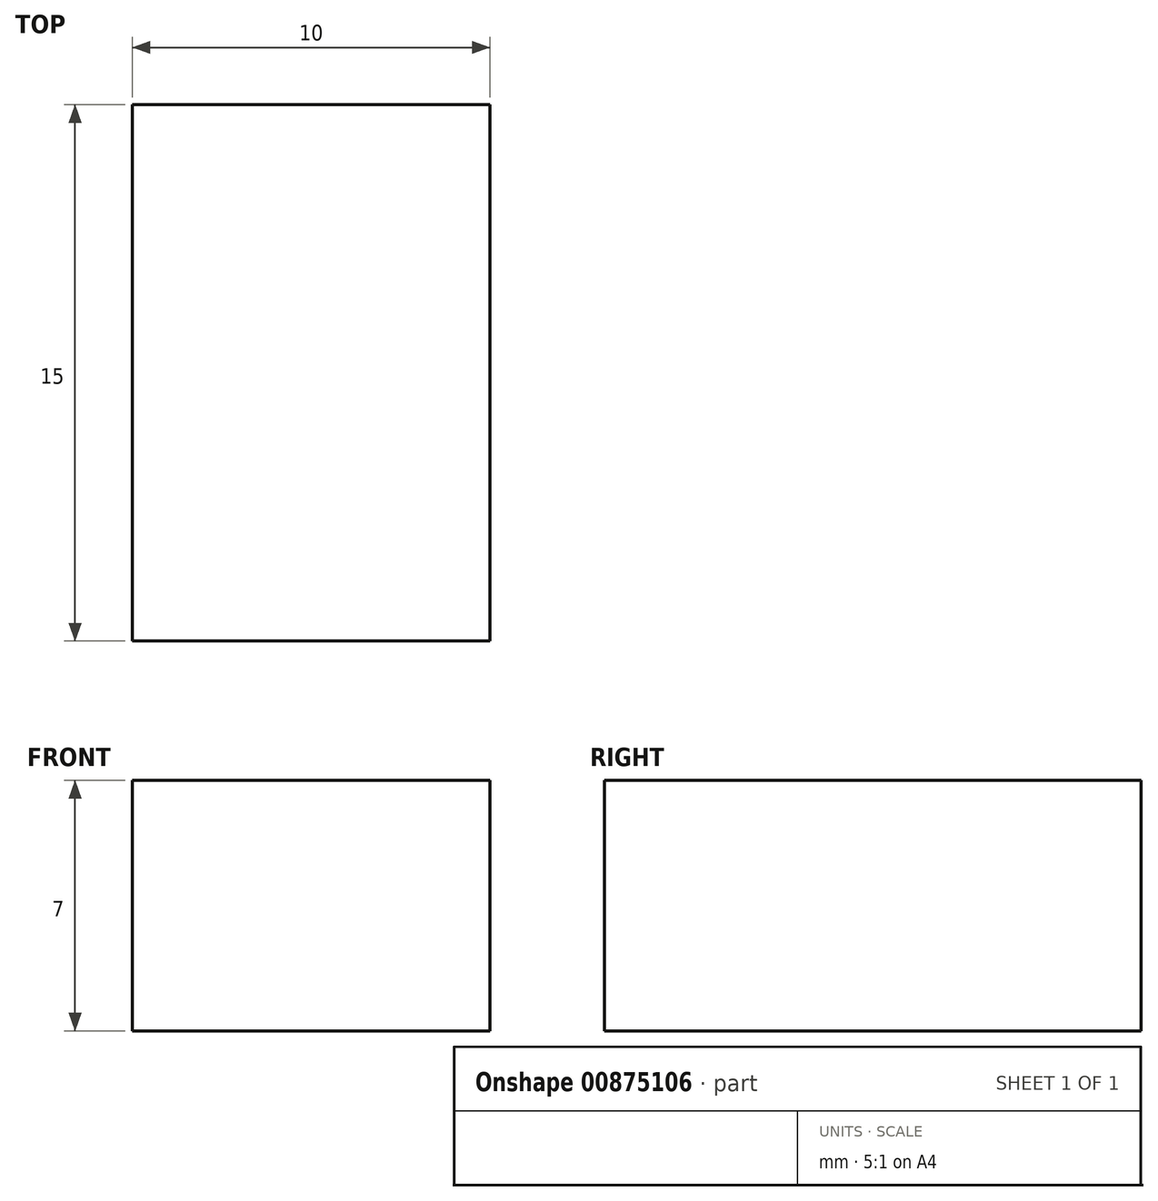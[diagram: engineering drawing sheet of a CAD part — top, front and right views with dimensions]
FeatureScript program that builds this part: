
annotation { "Feature Type Name" : "Feature", "Feature Type Description" : "" }
export const myFeature = defineFeature(function(context is Context, id is Id, definition is map)
    precondition{}
    {
        {
            var Q0;
            Q0=qCreatedBy(makeId("Top.planeOp"),FACE);
            var sketch = newSketch(context, id + "F0", { "sketchPlane" : qUnion([Q0])});
            skLineSegment(sketch, "E0.bottom", {"start": v(0, 0) * mm, "end": v(10, 0) * mm});
            skLineSegment(sketch, "E0.top", {"start": v(0, -15) * mm, "end": v(10, -15) * mm});
            skLineSegment(sketch, "E0.left", {"start": v(0, 0) * mm, "end": v(0, -15) * mm});
            skLineSegment(sketch, "E0.right", {"start": v(10, 0) * mm, "end": v(10, -15) * mm});
            skSolve(sketch);
        }
        {
            var Q0;
            Q0 = qSketchRegion(id + "F0", true);
            extrude(context, id + "F1", {"entities" : qUnion([Q0]), "depth" : 7 * mm, "offsetDistance" : 25.4 * mm});
        }
    });
